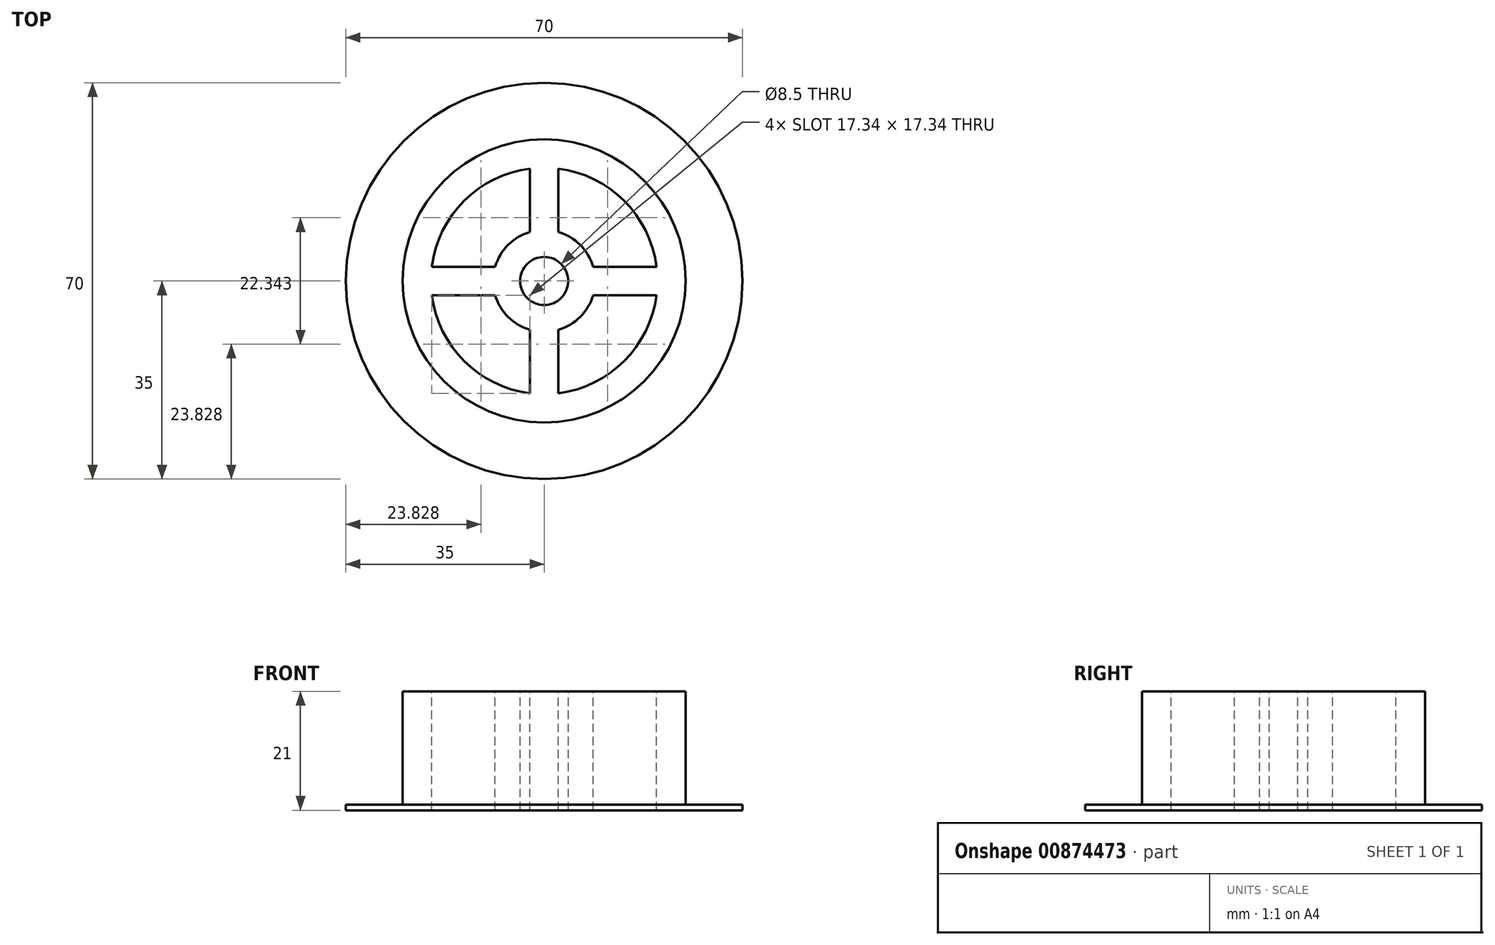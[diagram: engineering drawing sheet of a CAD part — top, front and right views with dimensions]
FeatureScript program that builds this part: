
annotation { "Feature Type Name" : "Feature", "Feature Type Description" : "" }
export const myFeature = defineFeature(function(context is Context, id is Id, definition is map)
    precondition{}
    {
        {
            var Q0;
            Q0=qCreatedBy(makeId("Top.planeOp"),FACE);
            var sketch = newSketch(context, id + "F0", { "sketchPlane" : qUnion([Q0])});
            skCircle(sketch, "E0", {"center": v(0, 0) * mm, "radius": 35 * mm});
            skSolve(sketch);
        }
        {
            var Q0;
            Q0=makeQuery(id+"F0.imprint","IMPRINT",FACE,{"disambiguationData":[TD([[makeQuery(id+"F0.imprint","IMPRINT",EDGE,{"derivedFrom":sQuery(id+"F0.wireOp",EDGE,"E0")}),1.0]])]});
            extrude(context, id + "F1", {"entities" : qUnion([Q0]), "depth" : 1 * mm, "offsetDistance" : 25 * mm});
        }
        {
            var Q0;
            Q0=makeQuery(id+"F1.opExtrude","CAP_FACE",FACE,{"disambiguationData":[OSD([sQuery(id+"F0.wireOp",EDGE,"E0")])],"isStart":false});
            var sketch = newSketch(context, id + "F2", { "sketchPlane" : qUnion([Q0])});
            skCircle(sketch, "E1", {"center": v(0, 0) * mm, "radius": 25 * mm});
            skSolve(sketch);
        }
        {
            var Q0;
            Q0=makeQuery(id+"F2.imprint","IMPRINT",FACE,{"disambiguationData":[TD([[makeQuery(id+"F2.imprint","IMPRINT",EDGE,{"derivedFrom":sQuery(id+"F2.wireOp",EDGE,"E1")}),1.0]])]});
            extrude(context, id + "F3", {"entities" : qUnion([Q0]), "operationType" : NewBodyOperationType.ADD, "depth" : 20 * mm, "offsetDistance" : 25 * mm});
        }
        {
            var Q0;
            Q0=makeQuery(id+"F3.opExtrude","CAP_FACE",FACE,{"disambiguationData":[OSD([sQuery(id+"F2.wireOp",EDGE,"E1")])],"isStart":false});
            var sketch = newSketch(context, id + "F4", { "sketchPlane" : qUnion([Q0])});
            skCircle(sketch, "E2", {"center": v(0, 0) * mm, "radius": 20 * mm});
            skCircle(sketch, "E3", {"center": v(0, 0) * mm, "radius": 4.25 * mm});
            skCircle(sketch, "E4", {"center": v(0, 0) * mm, "radius": 9 * mm});
            skLineSegment(sketch, "E5.bottom", {"start": v(2.5, 24.87) * mm, "end": v(-2.5, 24.87) * mm});
            skLineSegment(sketch, "E5.top", {"start": v(2.5, -24.87) * mm, "end": v(-2.5, -24.87) * mm});
            skLineSegment(sketch, "E5.left", {"start": v(2.5, 24.87) * mm, "end": v(2.5, 8.65) * mm});
            skLineSegment(sketch, "E5.right", {"start": v(-2.5, 24.87) * mm, "end": v(-2.5, 8.65) * mm});
            skLineSegment(sketch, "E6.bottom", {"start": v(24.87, -2.5) * mm, "end": v(8.65, -2.5) * mm});
            skLineSegment(sketch, "E6.top", {"start": v(24.87, 2.5) * mm, "end": v(8.65, 2.5) * mm});
            skLineSegment(sketch, "E6.left", {"start": v(24.87, -2.5) * mm, "end": v(24.87, 2.5) * mm});
            skLineSegment(sketch, "E6.right", {"start": v(-24.87, -2.5) * mm, "end": v(-24.87, 2.5) * mm});
            skLineSegment(sketch, "E7.trimOffspring", {"start": v(-8.65, 2.5) * mm, "end": v(-24.87, 2.5) * mm});
            skLineSegment(sketch, "E8.trimOffspring", {"start": v(-2.5, -8.65) * mm, "end": v(-2.5, -24.87) * mm});
            skLineSegment(sketch, "E9.trimOffspring", {"start": v(2.5, -8.65) * mm, "end": v(2.5, -24.87) * mm});
            skLineSegment(sketch, "E10.trimOffspring", {"start": v(-8.65, -2.5) * mm, "end": v(-24.87, -2.5) * mm});
            skSolve(sketch);
        }
        {
            var Q0;
            {var subQ0=sQuery(id+"F4.wireOp",EDGE,"E10.trimOffspring");var subQ1=sQuery(id+"F4.wireOp",EDGE,"E2");var subQ2=makeQuery(id+"F4.imprint","INTERSECT",VERTEX,{"derivedFrom":[subQ1,subQ0]});Q0=makeQuery(id+"F4.imprint","IMPRINT",FACE,{"disambiguationData":[TD([[makeQuery(id+"F4.imprint","IMPRINT",EDGE,{"disambiguationData":[TD([[subQ2,-1.0]])],"derivedFrom":subQ1}),1.0]])]});}
            var Q1;
            {var subQ0=sQuery(id+"F4.wireOp",EDGE,"E5.right");var subQ1=sQuery(id+"F4.wireOp",EDGE,"E2");var subQ2=makeQuery(id+"F4.imprint","INTERSECT",VERTEX,{"derivedFrom":[subQ1,subQ0]});Q1=makeQuery(id+"F4.imprint","IMPRINT",FACE,{"disambiguationData":[TD([[makeQuery(id+"F4.imprint","IMPRINT",EDGE,{"disambiguationData":[TD([[subQ2,-1.0]])],"derivedFrom":subQ1}),1.0]])]});}
            var Q2;
            {var subQ0=sQuery(id+"F4.wireOp",EDGE,"E5.left");var subQ1=sQuery(id+"F4.wireOp",EDGE,"E2");var subQ2=makeQuery(id+"F4.imprint","INTERSECT",VERTEX,{"derivedFrom":[subQ1,subQ0]});Q2=makeQuery(id+"F4.imprint","IMPRINT",FACE,{"disambiguationData":[TD([[makeQuery(id+"F4.imprint","IMPRINT",EDGE,{"disambiguationData":[TD([[subQ2,1.0]])],"derivedFrom":subQ1}),1.0]])]});}
            var Q3;
            {var subQ0=sQuery(id+"F4.wireOp",EDGE,"E9.trimOffspring");var subQ1=sQuery(id+"F4.wireOp",EDGE,"E2");var subQ2=makeQuery(id+"F4.imprint","INTERSECT",VERTEX,{"derivedFrom":[subQ1,subQ0]});Q3=makeQuery(id+"F4.imprint","IMPRINT",FACE,{"disambiguationData":[TD([[makeQuery(id+"F4.imprint","IMPRINT",EDGE,{"disambiguationData":[TD([[subQ2,-1.0]])],"derivedFrom":subQ1}),1.0]])]});}
            var Q4;
            Q4=makeQuery(id+"F4.imprint","IMPRINT",FACE,{"disambiguationData":[TD([[makeQuery(id+"F4.imprint","IMPRINT",EDGE,{"derivedFrom":sQuery(id+"F4.wireOp",EDGE,"E3")}),1.0]])]});
            extrude(context, id + "F5", {"entities" : qUnion([Q0, Q1, Q2, Q3, Q4]), "operationType" : NewBodyOperationType.REMOVE, "endBound" : BoundingType.UP_TO_NEXT, "oppositeDirection" : true, "depth" : 25 * mm, "offsetDistance" : 25 * mm});
        }
    });
